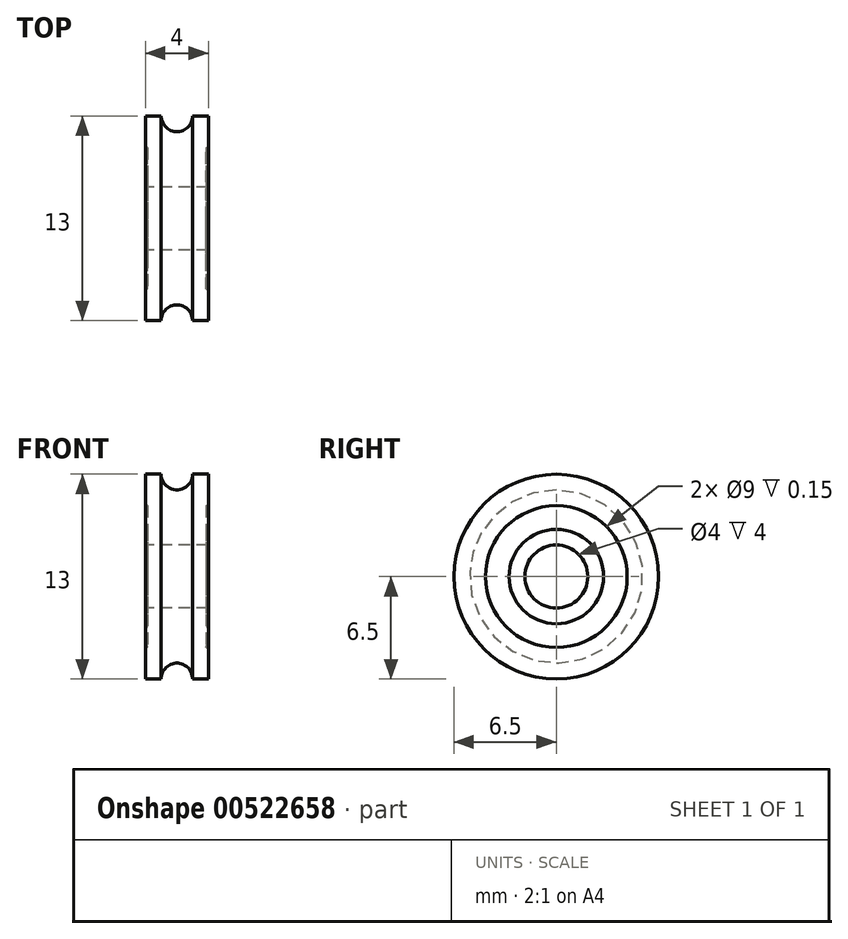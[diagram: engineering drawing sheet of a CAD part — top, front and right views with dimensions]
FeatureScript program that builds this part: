
annotation { "Feature Type Name" : "Feature", "Feature Type Description" : "" }
export const myFeature = defineFeature(function(context is Context, id is Id, definition is map)
    precondition{}
    {
        {
            var Q0;
            Q0=qCreatedBy(makeId("Front.planeOp"),FACE);
            var sketch = newSketch(context, id + "F0", { "sketchPlane" : qUnion([Q0])});
            skLineSegment(sketch, "E0", {"start": v(-17.08, 0) * mm, "end": v(16.32, 0) * mm, "construction": true});
            skLineSegment(sketch, "E1", {"start": v(0, 18.11) * mm, "end": v(0, -14.86) * mm, "construction": true});
            skLineSegment(sketch, "E2", {"start": v(0, 2) * mm, "end": v(-2, 2) * mm});
            skLineSegment(sketch, "E3", {"start": v(-2, 2) * mm, "end": v(-2, 3) * mm});
            skLineSegment(sketch, "E4", {"start": v(-2, 3) * mm, "end": v(-1.85, 3) * mm});
            skLineSegment(sketch, "E5", {"start": v(-1.85, 3) * mm, "end": v(-1.85, 4.5) * mm, "construction": true});
            skLineSegment(sketch, "E6", {"start": v(-1.85, 4.5) * mm, "end": v(-2, 4.5) * mm});
            skLineSegment(sketch, "E7", {"start": v(-2, 4.5) * mm, "end": v(-2, 6.5) * mm});
            skLineSegment(sketch, "E8", {"start": v(-2, 6.5) * mm, "end": v(-1, 6.5) * mm});
            skArc(sketch, "E9", {"start": v(-1, 6.5) * mm, "mid": v(-0.7, 5.8) * mm, "end": v(0, 5.5) * mm});
            skArc(sketch, "E10", {"start": v(-1.85, 4.5) * mm, "mid": v(-2, 3.75) * mm, "end": v(-1.85, 3) * mm});
            skLineSegment(sketch, "E11", {"start": v(0, 5.5) * mm, "end": v(0, 2) * mm});
            skSolve(sketch);
        }
        {
            var Q0;
            Q0=qSketchRegion(id+"F0",true);
            var Q1;
            Q1=sQuery(id+"F0.wireOp",EDGE,"E0");
            revolve(context, id + "F1", {"entities" : qUnion([Q0]), "axis" : qUnion([Q1]), "revolveType" : RevolveType.FULL});
        }
        {
            var Q0;
            Q0=makeQuery(id+"F1.opRevolve","SWEPT_BODY",BODY,{"disambiguationData":[OSD([sQuery(id+"F0.wireOp",EDGE,"E2"),sQuery(id+"F0.wireOp",EDGE,"E3"),sQuery(id+"F0.wireOp",EDGE,"E4"),sQuery(id+"F0.wireOp",EDGE,"E6"),sQuery(id+"F0.wireOp",EDGE,"E7"),sQuery(id+"F0.wireOp",EDGE,"E8"),sQuery(id+"F0.wireOp",EDGE,"E9"),sQuery(id+"F0.wireOp",EDGE,"E10"),sQuery(id+"F0.wireOp",EDGE,"E11")])]});
            var Q1;
            Q1=makeQuery(id+"F1.opRevolve","SWEPT_FACE",FACE,{"disambiguationData":[OSD([sQuery(id+"F0.wireOp",EDGE,"E11")])]});
            mirror(context, id + "F2", {"operationType" : NewBodyOperationType.ADD, "entities" : qUnion([Q0]), "mirrorPlane" : qUnion([Q1])});
        }
    });
